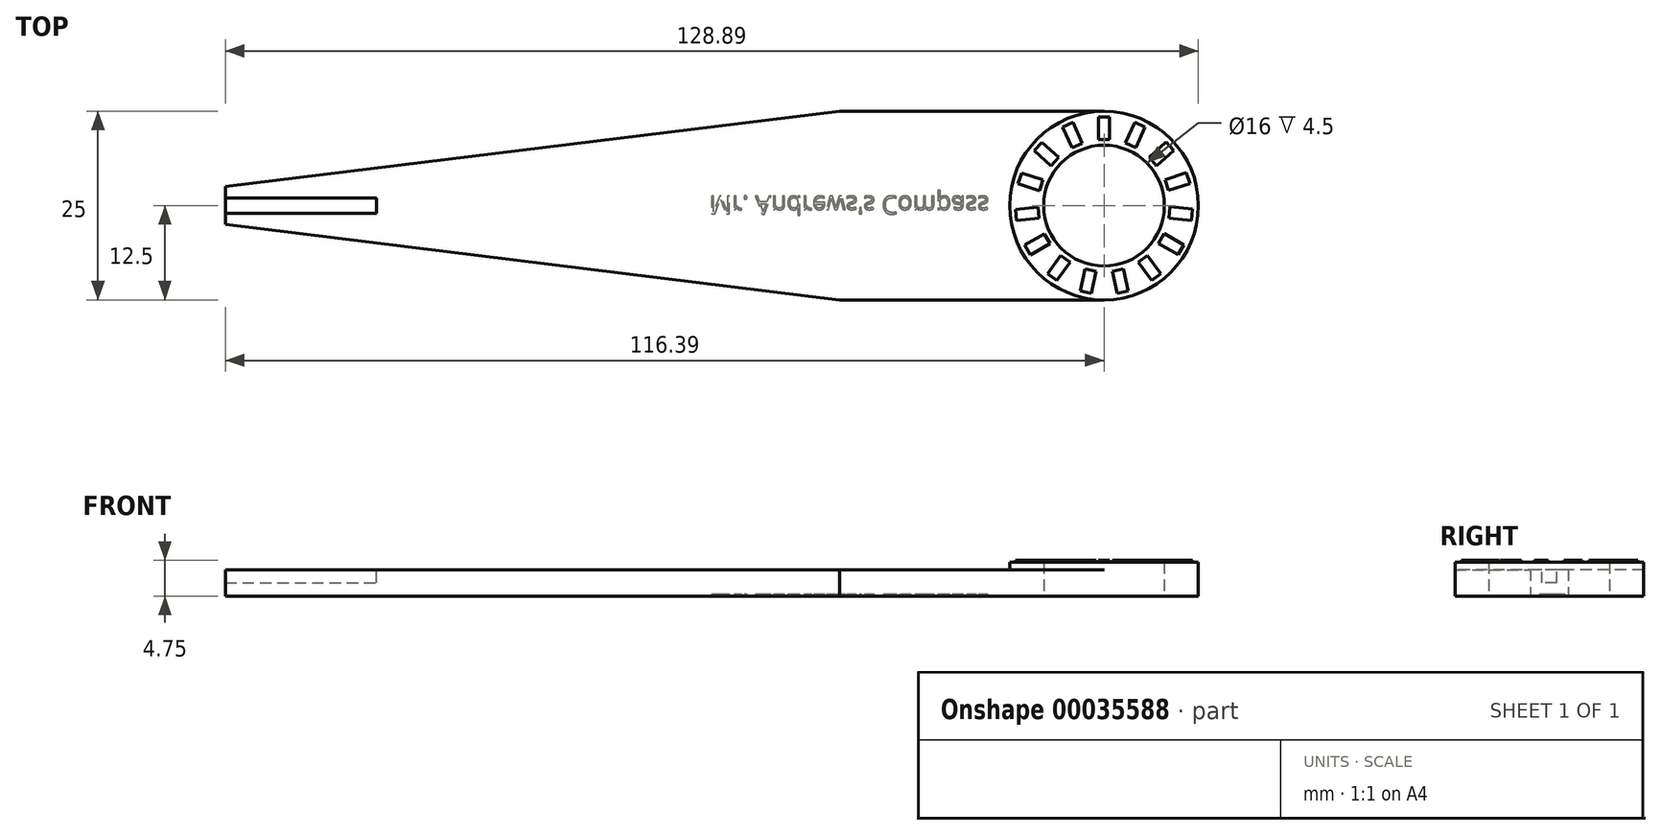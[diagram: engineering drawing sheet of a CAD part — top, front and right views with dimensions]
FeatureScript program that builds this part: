
annotation { "Feature Type Name" : "Feature", "Feature Type Description" : "" }
export const myFeature = defineFeature(function(context is Context, id is Id, definition is map)
    precondition{}
    {
        {
            var Q0;
            Q0=qCreatedBy(makeId("Top.planeOp"),FACE);
            var sketch = newSketch(context, id + "F0", { "sketchPlane" : qUnion([Q0])});
            skCircle(sketch, "E0", {"center": v(0, 0) * mm, "radius": 8 * mm});
            skCircle(sketch, "E1", {"center": v(0, 0) * mm, "radius": 12.5 * mm});
            skLineSegment(sketch, "E2", {"start": v(-35, 12.5) * mm, "end": v(0, 12.5) * mm});
            skLineSegment(sketch, "E3", {"start": v(-35, -12.5) * mm, "end": v(0, -12.5) * mm});
            skLineSegment(sketch, "E4", {"start": v(-35, 12.5) * mm, "end": v(-93.64, 12.5) * mm, "construction": true});
            skLineSegment(sketch, "E5", {"start": v(-35, 12.5) * mm, "end": v(-116.39, 2.5) * mm});
            skLineSegment(sketch, "E6", {"start": v(-35, -12.5) * mm, "end": v(-94.55, -12.5) * mm, "construction": true});
            skLineSegment(sketch, "E7", {"start": v(-35, -12.5) * mm, "end": v(-116.39, -2.5) * mm});
            skLineSegment(sketch, "E8", {"start": v(-116.39, 2.5) * mm, "end": v(-116.39, -2.5) * mm});
            skSolve(sketch);
        }
        {
            var Q0;
            Q0=qSketchRegion(id+"F0",true);
            extrude(context, id + "F1", {"entities" : qUnion([Q0]), "depth" : 3.5 * mm});
        }
        {
            var Q0;
            Q0=makeQuery(id+"F1.opExtrude","CAP_FACE",FACE,{"disambiguationData":[OSD([sQuery(id+"F0.wireOp",EDGE,"E0"),sQuery(id+"F0.wireOp",EDGE,"E1"),sQuery(id+"F0.wireOp",EDGE,"E2"),sQuery(id+"F0.wireOp",EDGE,"E3"),sQuery(id+"F0.wireOp",EDGE,"E5"),sQuery(id+"F0.wireOp",EDGE,"E7"),sQuery(id+"F0.wireOp",EDGE,"E8")])],"isStart":false});
            var sketch = newSketch(context, id + "F2", { "sketchPlane" : qUnion([Q0])});
            skCircle(sketch, "E9", {"center": v(0, 0) * mm, "radius": 12.5 * mm});
            skCircle(sketch, "E10", {"center": v(0, 0) * mm, "radius": 8 * mm});
            skSolve(sketch);
        }
        {
            var Q0;
            Q0=qSketchRegion(id+"F2",true);
            extrude(context, id + "F3", {"entities" : qUnion([Q0]), "operationType" : NewBodyOperationType.ADD, "depth" : 1 * mm});
        }
        {
            var Q0;
            Q0=makeQuery(id+"F1.opExtrude","CAP_FACE",FACE,{"disambiguationData":[OSD([sQuery(id+"F0.wireOp",EDGE,"E0"),sQuery(id+"F0.wireOp",EDGE,"E1"),sQuery(id+"F0.wireOp",EDGE,"E2"),sQuery(id+"F0.wireOp",EDGE,"E3"),sQuery(id+"F0.wireOp",EDGE,"E5"),sQuery(id+"F0.wireOp",EDGE,"E7"),sQuery(id+"F0.wireOp",EDGE,"E8")])],"isStart":false});
            var sketch = newSketch(context, id + "F4", { "sketchPlane" : qUnion([Q0])});
            skLineSegment(sketch, "E11.bottom", {"start": v(-116.39, 1) * mm, "end": v(-96.39, 1) * mm});
            skLineSegment(sketch, "E11.top", {"start": v(-116.39, -1) * mm, "end": v(-96.39, -1) * mm});
            skLineSegment(sketch, "E11.left", {"start": v(-116.39, 1) * mm, "end": v(-116.39, -1) * mm});
            skLineSegment(sketch, "E11.right", {"start": v(-96.39, 1) * mm, "end": v(-96.39, -1) * mm});
            skSolve(sketch);
        }
        {
            var Q0;
            Q0=qSketchRegion(id+"F4",true);
            extrude(context, id + "F5", {"entities" : qUnion([Q0]), "operationType" : NewBodyOperationType.REMOVE, "oppositeDirection" : true, "depth" : 1.75 * mm});
        }
        {
            var Q0;
            Q0=makeQuery(id+"F3.opExtrude","CAP_FACE",FACE,{"disambiguationData":[OSD([sQuery(id+"F2.wireOp",EDGE,"E9"),sQuery(id+"F2.wireOp",EDGE,"E10")])],"isStart":false});
            var sketch = newSketch(context, id + "F6", { "sketchPlane" : qUnion([Q0])});
            skLineSegment(sketch, "E12.bottom", {"start": v(-0.77, 11.73) * mm, "end": v(0.73, 11.73) * mm});
            skLineSegment(sketch, "E12.top", {"start": v(-0.77, 8.73) * mm, "end": v(0.73, 8.73) * mm});
            skLineSegment(sketch, "E12.left", {"start": v(-0.77, 11.73) * mm, "end": v(-0.77, 8.73) * mm});
            skLineSegment(sketch, "E12.right", {"start": v(0.73, 11.73) * mm, "end": v(0.73, 8.73) * mm});
            skLineSegment(sketch, "E13.1.0", {"start": v(-5.47, 10.4) * mm, "end": v(-4.25, 7.66) * mm});
            skLineSegment(sketch, "E13.1.1", {"start": v(-5.47, 10.4) * mm, "end": v(-4.1, 11.01) * mm});
            skLineSegment(sketch, "E13.1.2", {"start": v(-4.1, 11.01) * mm, "end": v(-2.88, 8.27) * mm});
            skLineSegment(sketch, "E13.1.3", {"start": v(-4.25, 7.66) * mm, "end": v(-2.88, 8.27) * mm});
            skLineSegment(sketch, "E13.2.0", {"start": v(-9.23, 7.28) * mm, "end": v(-7, 5.27) * mm});
            skLineSegment(sketch, "E13.2.1", {"start": v(-9.23, 7.28) * mm, "end": v(-8.22, 8.4) * mm});
            skLineSegment(sketch, "E13.2.2", {"start": v(-8.22, 8.4) * mm, "end": v(-6, 6.38) * mm});
            skLineSegment(sketch, "E13.2.3", {"start": v(-7, 5.27) * mm, "end": v(-6, 6.38) * mm});
            skLineSegment(sketch, "E13.3.0", {"start": v(-11.39, 2.9) * mm, "end": v(-8.53, 1.97) * mm});
            skLineSegment(sketch, "E13.3.1", {"start": v(-11.39, 2.9) * mm, "end": v(-10.92, 4.32) * mm});
            skLineSegment(sketch, "E13.3.2", {"start": v(-10.92, 4.32) * mm, "end": v(-8.07, 3.4) * mm});
            skLineSegment(sketch, "E13.3.3", {"start": v(-8.53, 1.97) * mm, "end": v(-8.07, 3.4) * mm});
            skLineSegment(sketch, "E13.4.0", {"start": v(-11.58, -1.99) * mm, "end": v(-8.6, -1.67) * mm});
            skLineSegment(sketch, "E13.4.1", {"start": v(-11.58, -1.99) * mm, "end": v(-11.74, -0.5) * mm});
            skLineSegment(sketch, "E13.4.2", {"start": v(-11.74, -0.5) * mm, "end": v(-8.75, -0.18) * mm});
            skLineSegment(sketch, "E13.4.3", {"start": v(-8.6, -1.67) * mm, "end": v(-8.75, -0.18) * mm});
            skLineSegment(sketch, "E13.5.0", {"start": v(-9.77, -6.53) * mm, "end": v(-7.17, -5.03) * mm});
            skLineSegment(sketch, "E13.5.1", {"start": v(-9.77, -6.53) * mm, "end": v(-10.52, -5.23) * mm});
            skLineSegment(sketch, "E13.5.2", {"start": v(-10.52, -5.23) * mm, "end": v(-7.92, -3.73) * mm});
            skLineSegment(sketch, "E13.5.3", {"start": v(-7.17, -5.03) * mm, "end": v(-7.92, -3.73) * mm});
            skLineSegment(sketch, "E13.6.0", {"start": v(-6.27, -9.94) * mm, "end": v(-4.5, -7.5) * mm});
            skLineSegment(sketch, "E13.6.1", {"start": v(-6.27, -9.94) * mm, "end": v(-7.49, -9.05) * mm});
            skLineSegment(sketch, "E13.6.2", {"start": v(-7.49, -9.05) * mm, "end": v(-5.72, -6.63) * mm});
            skLineSegment(sketch, "E13.6.3", {"start": v(-4.5, -7.5) * mm, "end": v(-5.72, -6.63) * mm});
            skLineSegment(sketch, "E13.7.0", {"start": v(-1.69, -11.63) * mm, "end": v(-1.07, -8.7) * mm});
            skLineSegment(sketch, "E13.7.1", {"start": v(-1.69, -11.63) * mm, "end": v(-3.16, -11.32) * mm});
            skLineSegment(sketch, "E13.7.2", {"start": v(-3.16, -11.32) * mm, "end": v(-2.53, -8.38) * mm});
            skLineSegment(sketch, "E13.7.3", {"start": v(-1.07, -8.7) * mm, "end": v(-2.53, -8.38) * mm});
            skLineSegment(sketch, "E13.8.0", {"start": v(3.19, -11.3) * mm, "end": v(2.56, -8.38) * mm});
            skLineSegment(sketch, "E13.8.1", {"start": v(3.19, -11.3) * mm, "end": v(1.72, -11.62) * mm});
            skLineSegment(sketch, "E13.8.2", {"start": v(1.72, -11.62) * mm, "end": v(1.1, -8.69) * mm});
            skLineSegment(sketch, "E13.8.3", {"start": v(2.56, -8.38) * mm, "end": v(1.1, -8.69) * mm});
            skLineSegment(sketch, "E13.9.0", {"start": v(7.51, -9.04) * mm, "end": v(5.75, -6.6) * mm});
            skLineSegment(sketch, "E13.9.1", {"start": v(7.51, -9.04) * mm, "end": v(6.3, -9.92) * mm});
            skLineSegment(sketch, "E13.9.2", {"start": v(6.3, -9.92) * mm, "end": v(4.53, -7.5) * mm});
            skLineSegment(sketch, "E13.9.3", {"start": v(5.75, -6.6) * mm, "end": v(4.53, -7.5) * mm});
            skLineSegment(sketch, "E13.10.0", {"start": v(10.54, -5.2) * mm, "end": v(7.94, -3.7) * mm});
            skLineSegment(sketch, "E13.10.1", {"start": v(10.54, -5.2) * mm, "end": v(9.79, -6.5) * mm});
            skLineSegment(sketch, "E13.10.2", {"start": v(9.79, -6.5) * mm, "end": v(7.19, -5) * mm});
            skLineSegment(sketch, "E13.10.3", {"start": v(7.94, -3.7) * mm, "end": v(7.19, -5) * mm});
            skLineSegment(sketch, "E13.11.0", {"start": v(11.74, -0.46) * mm, "end": v(8.76, -0.15) * mm});
            skLineSegment(sketch, "E13.11.1", {"start": v(11.74, -0.46) * mm, "end": v(11.58, -1.96) * mm});
            skLineSegment(sketch, "E13.11.2", {"start": v(11.58, -1.96) * mm, "end": v(8.6, -1.64) * mm});
            skLineSegment(sketch, "E13.11.3", {"start": v(8.76, -0.15) * mm, "end": v(8.6, -1.64) * mm});
            skLineSegment(sketch, "E13.12.0", {"start": v(10.91, 4.35) * mm, "end": v(8.06, 3.42) * mm});
            skLineSegment(sketch, "E13.12.1", {"start": v(10.91, 4.35) * mm, "end": v(11.38, 2.92) * mm});
            skLineSegment(sketch, "E13.12.2", {"start": v(11.38, 2.92) * mm, "end": v(8.53, 2) * mm});
            skLineSegment(sketch, "E13.12.3", {"start": v(8.06, 3.42) * mm, "end": v(8.53, 2) * mm});
            skLineSegment(sketch, "E13.13.0", {"start": v(8.2, 8.41) * mm, "end": v(5.97, 6.4) * mm});
            skLineSegment(sketch, "E13.13.1", {"start": v(8.2, 8.41) * mm, "end": v(9.2, 7.3) * mm});
            skLineSegment(sketch, "E13.13.2", {"start": v(9.2, 7.3) * mm, "end": v(6.98, 5.3) * mm});
            skLineSegment(sketch, "E13.13.3", {"start": v(5.97, 6.4) * mm, "end": v(6.98, 5.3) * mm});
            skLineSegment(sketch, "E13.14.0", {"start": v(4.07, 11.02) * mm, "end": v(2.85, 8.28) * mm});
            skLineSegment(sketch, "E13.14.1", {"start": v(4.07, 11.02) * mm, "end": v(5.44, 10.41) * mm});
            skLineSegment(sketch, "E13.14.2", {"start": v(5.44, 10.41) * mm, "end": v(4.22, 7.67) * mm});
            skLineSegment(sketch, "E13.14.3", {"start": v(2.85, 8.28) * mm, "end": v(4.22, 7.67) * mm});
            skPoint(sketch, "E13.center", {"position": v(0, 0) * mm});
            skSolve(sketch);
        }
        {
            var Q0;
            Q0=qSketchRegion(id+"F6",true);
            extrude(context, id + "F7", {"entities" : qUnion([Q0]), "operationType" : NewBodyOperationType.ADD, "depth" : .25 * mm});
        }
        {
            var Q0;
            Q0=makeQuery(id+"F1.opExtrude","CAP_FACE",FACE,{"disambiguationData":[OSD([sQuery(id+"F0.wireOp",EDGE,"E0"),sQuery(id+"F0.wireOp",EDGE,"E1"),sQuery(id+"F0.wireOp",EDGE,"E2"),sQuery(id+"F0.wireOp",EDGE,"E3"),sQuery(id+"F0.wireOp",EDGE,"E5"),sQuery(id+"F0.wireOp",EDGE,"E7"),sQuery(id+"F0.wireOp",EDGE,"E8")])],"isStart":true});
            var sketch = newSketch(context, id + "F8", { "sketchPlane" : qUnion([Q0])});
            skText(sketch, "E14", { "text": "Mr. Andrews\'s Compass", "fontName": "OpenSans-Regular.ttf"});
            const initialGuessF8  = {"E14": [-0.05229, -0.00125, 1, 0, 0.00239]};
            skSetInitialGuess(sketch, initialGuessF8);
            skSolve(sketch);
        }
        {
            var Q0;
            Q0=qSketchRegion(id+"F8",true);
            extrude(context, id + "F9", {"entities" : qUnion([Q0]), "operationType" : NewBodyOperationType.REMOVE, "oppositeDirection" : true, "depth" : .25 * mm});
        }
    });
